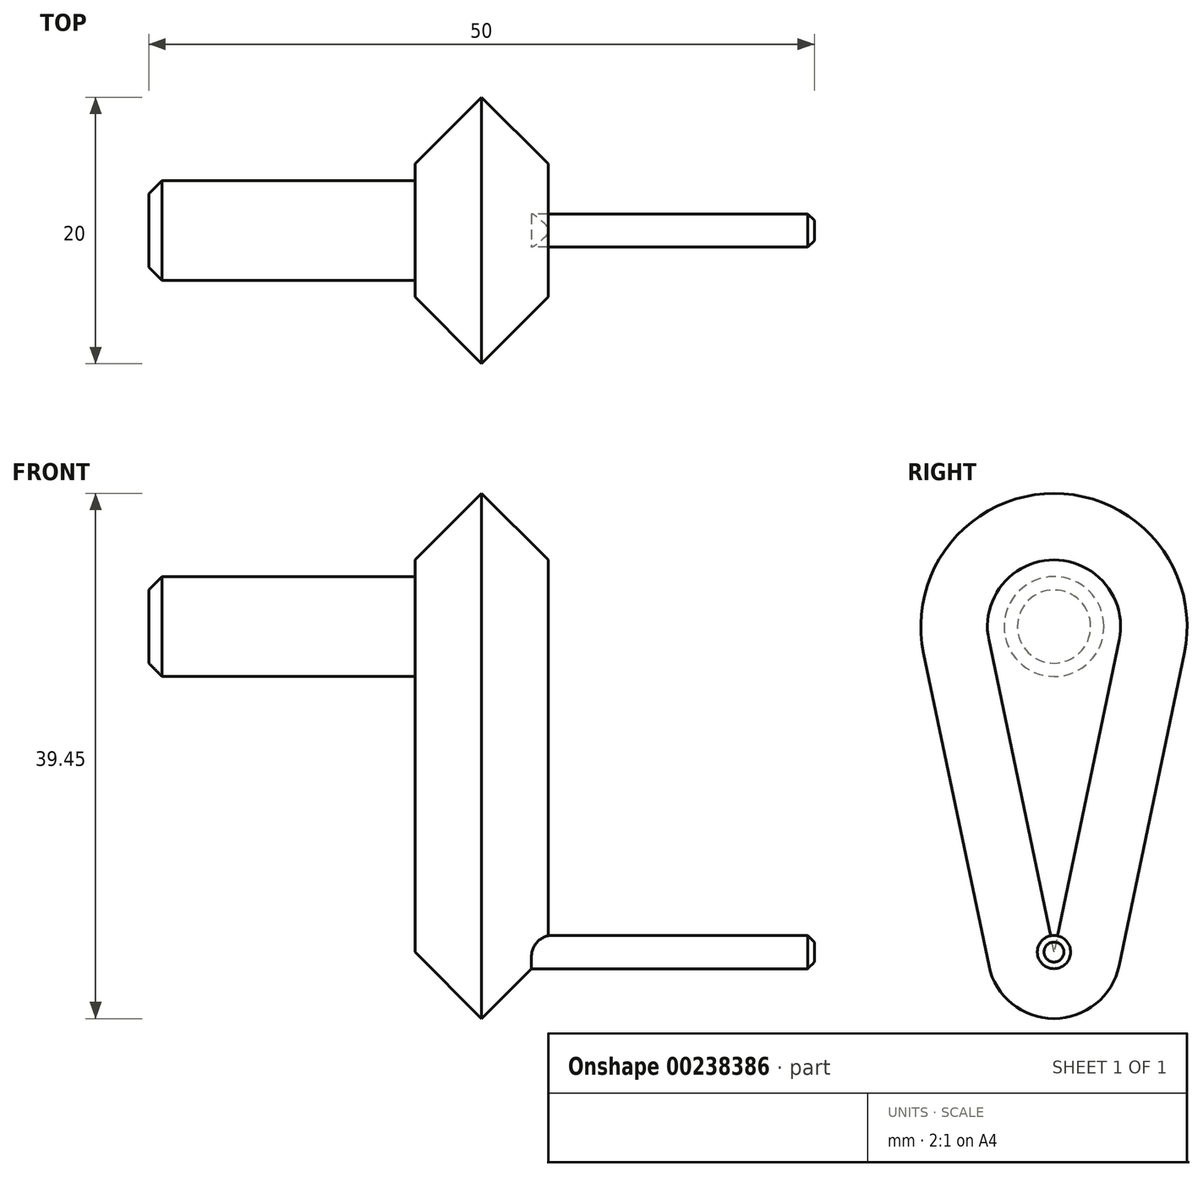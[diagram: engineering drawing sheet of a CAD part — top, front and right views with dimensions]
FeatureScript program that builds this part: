
annotation { "Feature Type Name" : "Feature", "Feature Type Description" : "" }
export const myFeature = defineFeature(function(context is Context, id is Id, definition is map)
    precondition{}
    {
        {
            var Q0;
            Q0=qCreatedBy(makeId("Right.planeOp"),FACE);
            var sketch = newSketch(context, id + "F0", { "sketchPlane" : qUnion([Q0])});
            skCircle(sketch, "E0", {"center": v(-6.1, 21.27) * mm, "radius": 10 * mm});
            skCircle(sketch, "E1", {"center": v(-6.1, -3.18) * mm, "radius": 5 * mm});
            skLineSegment(sketch, "E2", {"start": v(-15.89, 19.23) * mm, "end": v(-11, -4.2) * mm});
            skLineSegment(sketch, "E3", {"start": v(3.7, 19.23) * mm, "end": v(-1.2, -4.2) * mm});
            skCircle(sketch, "E4", {"center": v(-6.1, 21.27) * mm, "radius": 3.75 * mm});
            skCircle(sketch, "E5", {"center": v(-6.1, -3.18) * mm, "radius": 1.25 * mm});
            skSolve(sketch);
        }
        {
            var Q0;
            Q0=makeQuery(id+"F0.imprint","IMPRINT",FACE,{"disambiguationData":[TD([[makeQuery(id+"F0.imprint","IMPRINT",EDGE,{"derivedFrom":sQuery(id+"F0.wireOp",EDGE,"E4")}),-1.0]])]});
            var Q1;
            {var subQ0=sQuery(id+"F0.wireOp",EDGE,"E2");Q1=makeQuery(id+"F0.imprint","IMPRINT",FACE,{"disambiguationData":[TD([[makeQuery(id+"F0.imprint","IMPRINT",EDGE,{"derivedFrom":subQ0}),1.0]])]});}
            var Q2;
            Q2=makeQuery(id+"F0.imprint","IMPRINT",FACE,{"disambiguationData":[TD([[makeQuery(id+"F0.imprint","IMPRINT",EDGE,{"derivedFrom":sQuery(id+"F0.wireOp",EDGE,"E4")}),1.0]])]});
            var Q3;
            Q3=makeQuery(id+"F0.imprint","IMPRINT",FACE,{"disambiguationData":[TD([[makeQuery(id+"F0.imprint","IMPRINT",EDGE,{"derivedFrom":sQuery(id+"F0.wireOp",EDGE,"E5")}),1.0]])]});
            var Q4;
            Q4=makeQuery(id+"F0.imprint","IMPRINT",FACE,{"disambiguationData":[TD([[makeQuery(id+"F0.imprint","IMPRINT",EDGE,{"derivedFrom":sQuery(id+"F0.wireOp",EDGE,"E5")}),-1.0]])]});
            extrude(context, id + "F1", {"entities" : qUnion([Q0, Q1, Q2, Q3, Q4]), "depth" : 10 * mm});
        }
        {
            var Q0;
            Q0=makeQuery(id+"F0.imprint","IMPRINT",FACE,{"disambiguationData":[TD([[makeQuery(id+"F0.imprint","IMPRINT",EDGE,{"derivedFrom":sQuery(id+"F0.wireOp",EDGE,"E4")}),1.0]])]});
            extrude(context, id + "F2", {"entities" : qUnion([Q0]), "operationType" : NewBodyOperationType.ADD, "oppositeDirection" : true, "depth" : 20 * mm});
        }
        {
            var Q0;
            Q0=makeQuery(id+"F0.imprint","IMPRINT",FACE,{"disambiguationData":[TD([[makeQuery(id+"F0.imprint","IMPRINT",EDGE,{"derivedFrom":sQuery(id+"F0.wireOp",EDGE,"E5")}),1.0]])]});
            extrude(context, id + "F3", {"entities" : qUnion([Q0]), "operationType" : NewBodyOperationType.ADD, "depth" : 30 * mm});
        }
        {
            var Q0;
            Q0=makeQuery(id+"F1.opExtrude","CAP_EDGE",EDGE,{"disambiguationData":[OSD([sQuery(id+"F0.wireOp",EDGE,"E3")])],"isStart":true});
            var Q1;
            Q1=makeQuery(id+"F1.opExtrude","CAP_EDGE",EDGE,{"disambiguationData":[OSD([sQuery(id+"F0.wireOp",EDGE,"E3")])],"isStart":false});
            chamfer(context, id + "F4", {"entities" : qUnion([Q0, Q1]), "width" : 5 * mm, "tangentPropagation" : true});
        }
        {
            var Q0;
            Q0=makeQuery(id+"F2.opExtrude","CAP_EDGE",EDGE,{"disambiguationData":[OSD([sQuery(id+"F0.wireOp",EDGE,"E4")])],"isStart":false});
            chamfer(context, id + "F5", {"entities" : qUnion([Q0]), "width" : 1 * mm, "tangentPropagation" : true});
        }
        {
            var Q0;
            Q0=makeQuery(id+"F3.opExtrude","CAP_EDGE",EDGE,{"disambiguationData":[OSD([sQuery(id+"F0.wireOp",EDGE,"E5")])],"isStart":false});
            chamfer(context, id + "F6", {"entities" : qUnion([Q0]), "width" : 0.5 * mm, "tangentPropagation" : true});
        }
    });
